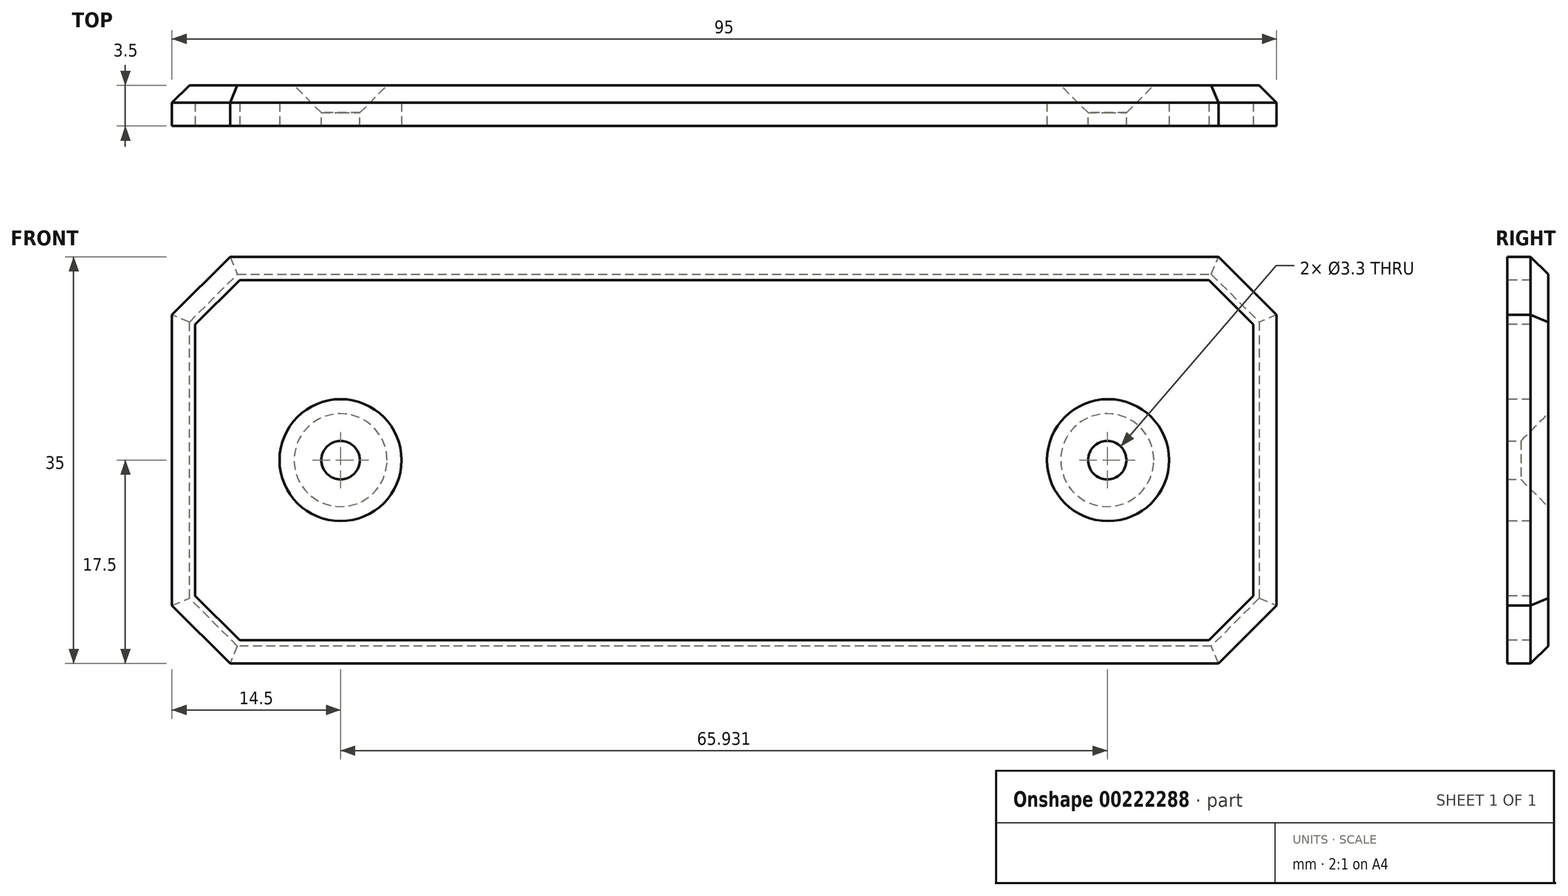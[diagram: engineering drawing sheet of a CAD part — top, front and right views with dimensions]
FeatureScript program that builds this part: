
annotation { "Feature Type Name" : "Feature", "Feature Type Description" : "" }
export const myFeature = defineFeature(function(context is Context, id is Id, definition is map)
    precondition{}
    {
        {
            var Q0;
            Q0=qCreatedBy(makeId("Front.planeOp"),FACE);
            var sketch = newSketch(context, id + "F0", { "sketchPlane" : qUnion([Q0])});
            skLineSegment(sketch, "E0", {"start": v(0, 36.91) * mm, "end": v(0, -44.56) * mm, "construction": true});
            skLineSegment(sketch, "E1", {"start": v(-51.32, 0) * mm, "end": v(51.77, 0) * mm, "construction": true});
            skLineSegment(sketch, "E2", {"start": v(-47.5, -17.5) * mm, "end": v(-47.5, 17.5) * mm});
            skLineSegment(sketch, "E3", {"start": v(-47.5, 17.5) * mm, "end": v(47.5, 17.5) * mm});
            skLineSegment(sketch, "E4", {"start": v(47.5, 17.5) * mm, "end": v(47.5, -17.5) * mm});
            skLineSegment(sketch, "E5", {"start": v(47.5, -17.5) * mm, "end": v(-47.5, -17.5) * mm});
            skSolve(sketch);
        }
        {
            var Q0;
            Q0=makeQuery(id+"F0.imprint","IMPRINT",FACE,{"disambiguationData":[TD([[makeQuery(id+"F0.imprint","IMPRINT",EDGE,{"derivedFrom":sQuery(id+"F0.wireOp",EDGE,"E2")}),-1.0]])]});
            extrude(context, id + "F1", {"entities" : qUnion([Q0]), "depth" : 3.5 * mm});
        }
        {
            var Q0;
            Q0=makeQuery(id+"F1.opExtrude","SWEPT_EDGE",EDGE,{"disambiguationData":[OSD([sQuery(id+"F0.wireOp",EDGE,"E4"),sQuery(id+"F0.wireOp",EDGE,"E5")])]});
            var Q1;
            Q1=makeQuery(id+"F1.opExtrude","SWEPT_EDGE",EDGE,{"disambiguationData":[OSD([sQuery(id+"F0.wireOp",EDGE,"E3"),sQuery(id+"F0.wireOp",EDGE,"E4")])]});
            var Q2;
            Q2=makeQuery(id+"F1.opExtrude","SWEPT_EDGE",EDGE,{"disambiguationData":[OSD([sQuery(id+"F0.wireOp",EDGE,"E2"),sQuery(id+"F0.wireOp",EDGE,"E5")])]});
            var Q3;
            Q3=makeQuery(id+"F1.opExtrude","SWEPT_EDGE",EDGE,{"disambiguationData":[OSD([sQuery(id+"F0.wireOp",EDGE,"E2"),sQuery(id+"F0.wireOp",EDGE,"E3")])]});
            chamfer(context, id + "F2", {"entities" : qUnion([Q0, Q1, Q2, Q3]), "width" : 5 * mm, "tangentPropagation" : true});
        }
        {
            var Q0;
            Q0=makeQuery(id+"F1.opExtrude","CAP_FACE",FACE,{"disambiguationData":[OSD([sQuery(id+"F0.wireOp",EDGE,"E2"),sQuery(id+"F0.wireOp",EDGE,"E3"),sQuery(id+"F0.wireOp",EDGE,"E4"),sQuery(id+"F0.wireOp",EDGE,"E5")])],"isStart":false});
            var sketch = newSketch(context, id + "F3", { "sketchPlane" : qUnion([Q0])});
            skLineSegment(sketch, "E6.0", {"start": v(-41.67, 15.5) * mm, "end": v(-45.5, 11.67) * mm});
            skLineSegment(sketch, "E6.1", {"start": v(-45.5, -11.67) * mm, "end": v(-45.5, 11.67) * mm});
            skLineSegment(sketch, "E6.2", {"start": v(-41.67, 15.5) * mm, "end": v(41.67, 15.5) * mm});
            skLineSegment(sketch, "E6.3", {"start": v(-45.5, -11.67) * mm, "end": v(-41.67, -15.5) * mm});
            skLineSegment(sketch, "E6.4", {"start": v(45.5, 11.67) * mm, "end": v(41.67, 15.5) * mm});
            skLineSegment(sketch, "E6.5", {"start": v(45.5, 11.67) * mm, "end": v(45.5, -11.67) * mm});
            skLineSegment(sketch, "E6.6", {"start": v(41.67, -15.5) * mm, "end": v(45.5, -11.67) * mm});
            skLineSegment(sketch, "E6.7", {"start": v(41.67, -15.5) * mm, "end": v(-41.67, -15.5) * mm});
            skSolve(sketch);
        }
        {
            var Q0;
            Q0=makeQuery(id+"F3.imprint","IMPRINT",FACE,{"disambiguationData":[TD([[makeQuery(id+"F3.imprint","IMPRINT",EDGE,{"derivedFrom":sQuery(id+"F3.wireOp",EDGE,"E6.0")}),1.0]])]});
            extrude(context, id + "F4", {"entities" : qUnion([Q0]), "operationType" : NewBodyOperationType.REMOVE, "oppositeDirection" : true, "depth" : 2 * mm});
        }
        {
            var Q0;
            Q0=makeQuery(id+"F1.opExtrude","CAP_FACE",FACE,{"disambiguationData":[OSD([sQuery(id+"F0.wireOp",EDGE,"E2"),sQuery(id+"F0.wireOp",EDGE,"E3"),sQuery(id+"F0.wireOp",EDGE,"E4"),sQuery(id+"F0.wireOp",EDGE,"E5")])],"isStart":false});
            var sketch = newSketch(context, id + "F5", { "sketchPlane" : qUnion([Q0])});
            skLineSegment(sketch, "E7", {"start": v(0, 32.55) * mm, "end": v(0, -36.72) * mm, "construction": true});
            skCircle(sketch, "E8", {"center": v(33, 0) * mm, "radius": 5.25 * mm});
            skCircle(sketch, "E9", {"center": v(-33, 0) * mm, "radius": 5.25 * mm});
            skSolve(sketch);
        }
        {
            var Q0;
            Q0=makeQuery(id+"F1.opExtrude","CAP_FACE",FACE,{"disambiguationData":[OSD([sQuery(id+"F0.wireOp",EDGE,"E2"),sQuery(id+"F0.wireOp",EDGE,"E3"),sQuery(id+"F0.wireOp",EDGE,"E4"),sQuery(id+"F0.wireOp",EDGE,"E5")])],"isStart":true});
            var sketch = newSketch(context, id + "F6", { "sketchPlane" : qUnion([Q0])});
            skPoint(sketch, "E10", {"position": v(-32.93, 0) * mm});
            skPoint(sketch, "E11", {"position": v(33, 0) * mm});
            skSolve(sketch);
        }
        {
            var Q0;
            Q0=makeQuery(id+"F5.imprint","IMPRINT",FACE,{"disambiguationData":[TD([[makeQuery(id+"F5.imprint","IMPRINT",EDGE,{"derivedFrom":sQuery(id+"F5.wireOp",EDGE,"E8")}),1.0]])]});
            var Q1;
            Q1=makeQuery(id+"F5.imprint","IMPRINT",FACE,{"disambiguationData":[TD([[makeQuery(id+"F5.imprint","IMPRINT",EDGE,{"derivedFrom":sQuery(id+"F5.wireOp",EDGE,"E9")}),1.0]])]});
            extrude(context, id + "F7", {"entities" : qUnion([Q0, Q1]), "operationType" : NewBodyOperationType.ADD, "endBound" : BoundingType.UP_TO_NEXT, "oppositeDirection" : true, "depth" : 25 * mm});
        }
        {
            var Q0;
            Q0=sQuery(id+"F6.wireOp",VERTEX,"E11");
            var Q1;
            Q1=sQuery(id+"F6.wireOp",VERTEX,"E10");
            var Q2;
            Q2=makeQuery(id+"F1.opExtrude","SWEPT_BODY",BODY,{"disambiguationData":[OSD([sQuery(id+"F0.wireOp",EDGE,"E2"),sQuery(id+"F0.wireOp",EDGE,"E3"),sQuery(id+"F0.wireOp",EDGE,"E4"),sQuery(id+"F0.wireOp",EDGE,"E5")])]});
            hole(context, id + "F8", {"style" : HoleStyle.C_SINK, "endStyle" : HoleEndStyle.THROUGH, "holeDiameter" : 3.3 * mm, "cSinkDiameter" : 8 * mm, "cSinkAngle" : 90 * degree, "locations" : qUnion([Q0, Q1]), "scope" : qUnion([Q2]), "isTappedThrough" : true});
        }
        {
            var Q0;
            Q0=makeQuery(id+"F1.opExtrude","CAP_EDGE",EDGE,{"disambiguationData":[OSD([sQuery(id+"F0.wireOp",EDGE,"E5")])],"isStart":true});
            var Q1;
            {var subQ0=sQuery(id+"F0.wireOp",EDGE,"E5");var subQ1=sQuery(id+"F0.wireOp",EDGE,"E4");Q1=makeQuery(id+"F2.opChamfer","BLEND_EDGE",EDGE,{"blendedFrom":[makeQuery(id+"F1.opExtrude","SWEPT_EDGE",EDGE,{"disambiguationData":[OSD([subQ1,subQ0])]}),makeQuery(id+"F1.opExtrude","CAP_FACE",FACE,{"disambiguationData":[OSD([sQuery(id+"F0.wireOp",EDGE,"E2"),sQuery(id+"F0.wireOp",EDGE,"E3"),subQ1,subQ0])],"isStart":true})],"blendedInto":[makeQuery(id+"F1.opExtrude","CAP_FACE",FACE,{"disambiguationData":[OSD([sQuery(id+"F0.wireOp",EDGE,"E2"),sQuery(id+"F0.wireOp",EDGE,"E3"),subQ1,subQ0])],"isStart":true})]});}
            var Q2;
            Q2=makeQuery(id+"F1.opExtrude","CAP_EDGE",EDGE,{"disambiguationData":[OSD([sQuery(id+"F0.wireOp",EDGE,"E4")])],"isStart":true});
            var Q3;
            {var subQ0=sQuery(id+"F0.wireOp",EDGE,"E4");var subQ1=sQuery(id+"F0.wireOp",EDGE,"E3");Q3=makeQuery(id+"F2.opChamfer","BLEND_EDGE",EDGE,{"blendedFrom":[makeQuery(id+"F1.opExtrude","SWEPT_EDGE",EDGE,{"disambiguationData":[OSD([subQ1,subQ0])]}),makeQuery(id+"F1.opExtrude","CAP_FACE",FACE,{"disambiguationData":[OSD([sQuery(id+"F0.wireOp",EDGE,"E2"),subQ1,subQ0,sQuery(id+"F0.wireOp",EDGE,"E5")])],"isStart":true})],"blendedInto":[makeQuery(id+"F1.opExtrude","CAP_FACE",FACE,{"disambiguationData":[OSD([sQuery(id+"F0.wireOp",EDGE,"E2"),subQ1,subQ0,sQuery(id+"F0.wireOp",EDGE,"E5")])],"isStart":true})]});}
            var Q4;
            Q4=makeQuery(id+"F1.opExtrude","CAP_EDGE",EDGE,{"disambiguationData":[OSD([sQuery(id+"F0.wireOp",EDGE,"E3")])],"isStart":true});
            var Q5;
            {var subQ0=sQuery(id+"F0.wireOp",EDGE,"E3");var subQ1=sQuery(id+"F0.wireOp",EDGE,"E2");Q5=makeQuery(id+"F2.opChamfer","BLEND_EDGE",EDGE,{"blendedFrom":[makeQuery(id+"F1.opExtrude","SWEPT_EDGE",EDGE,{"disambiguationData":[OSD([subQ1,subQ0])]}),makeQuery(id+"F1.opExtrude","CAP_FACE",FACE,{"disambiguationData":[OSD([subQ1,subQ0,sQuery(id+"F0.wireOp",EDGE,"E4"),sQuery(id+"F0.wireOp",EDGE,"E5")])],"isStart":true})],"blendedInto":[makeQuery(id+"F1.opExtrude","CAP_FACE",FACE,{"disambiguationData":[OSD([subQ1,subQ0,sQuery(id+"F0.wireOp",EDGE,"E4"),sQuery(id+"F0.wireOp",EDGE,"E5")])],"isStart":true})]});}
            var Q6;
            {var subQ0=sQuery(id+"F0.wireOp",EDGE,"E5");var subQ1=sQuery(id+"F0.wireOp",EDGE,"E2");Q6=makeQuery(id+"F2.opChamfer","BLEND_EDGE",EDGE,{"blendedFrom":[makeQuery(id+"F1.opExtrude","SWEPT_EDGE",EDGE,{"disambiguationData":[OSD([subQ1,subQ0])]}),makeQuery(id+"F1.opExtrude","CAP_FACE",FACE,{"disambiguationData":[OSD([subQ1,sQuery(id+"F0.wireOp",EDGE,"E3"),sQuery(id+"F0.wireOp",EDGE,"E4"),subQ0])],"isStart":true})],"blendedInto":[makeQuery(id+"F1.opExtrude","CAP_FACE",FACE,{"disambiguationData":[OSD([subQ1,sQuery(id+"F0.wireOp",EDGE,"E3"),sQuery(id+"F0.wireOp",EDGE,"E4"),subQ0])],"isStart":true})]});}
            var Q7;
            Q7=makeQuery(id+"F1.opExtrude","CAP_EDGE",EDGE,{"disambiguationData":[OSD([sQuery(id+"F0.wireOp",EDGE,"E2")])],"isStart":true});
            chamfer(context, id + "F9", {"entities" : qUnion([Q0, Q1, Q2, Q3, Q4, Q5, Q6, Q7]), "width" : 1.5 * mm, "tangentPropagation" : true});
        }
    });
